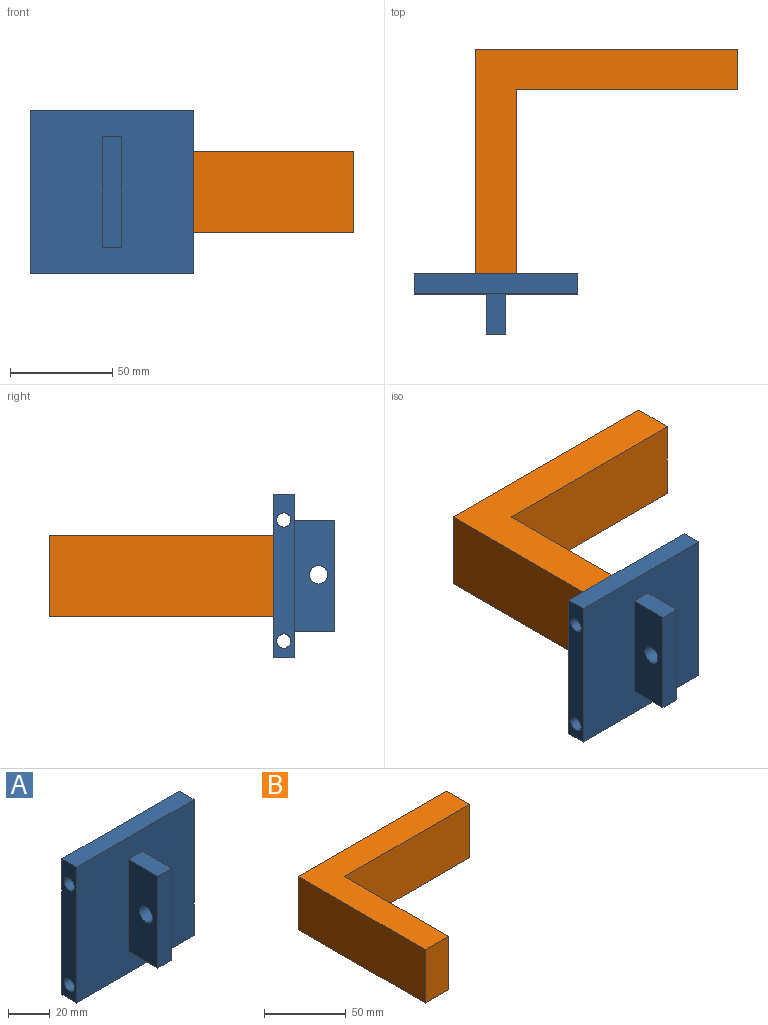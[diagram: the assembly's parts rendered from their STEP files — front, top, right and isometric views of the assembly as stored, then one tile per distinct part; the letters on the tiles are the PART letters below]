
ASSEMBLY  parts=2 mates=1
PART A: 14 faces, bbox 80x30x80 mm
  f0: plane 80x80mm, normal (0,-1,0), area 5884.6mm2, adj f1,f2,f3,f4,f6,f7,f8,f9
  f1: plane 80x10mm, normal (-1,0,0), area 723mm2, adj f0,f2,f4,f5,f11,f12
  f2: plane 80x10mm, normal (0,0,-1), area 800mm2, adj f0,f1,f3,f5
  f3: plane 80x10mm, normal (1,0,0), area 723mm2, adj f0,f2,f4,f5,f11,f12
  f4: plane 80x10mm, normal (0,0,1), area 800mm2, adj f0,f1,f3,f5
  f5: plane 80x80mm, normal (0,1,0), area 6400mm2, adj f1,f2,f3,f4
  f6: plane 54.11x20mm, normal (-1,0,0), area 1018.5mm2, adj f0,f7,f9,f10,f13
  f7: plane 20x9.53mm, normal (0,0,-1), area 190.5mm2, adj f0,f6,f8,f10
  f8: plane 54.11x20mm, normal (1,0,0), area 1018.5mm2, adj f0,f7,f9,f10,f13
  f9: plane 20x9.53mm, normal (0,0,1), area 190.5mm2, adj f0,f6,f8,f10
  f10: plane 54.11x9.53mm, normal (0,-1,0), area 515.4mm2, adj f6,f7,f8,f9
  f11: cylinder r=3.5mm len=80mm, axis (1,0,0), area 1759.3mm2, adj f1,f3
  f12: cylinder r=3.5mm len=80mm, axis (1,0,0), area 1759.3mm2, adj f1,f3
  f13: cylinder r=4.5mm len=9.53mm, axis (1,0,0), area 269.3mm2, adj f6,f8
PART B: 8 faces, bbox 128.4x110x40 mm
  f0: plane 110x40mm, normal (-1,0,0), area 4400mm2, adj f1,f5,f6,f7
  f1: plane 40x20mm, normal (0,-1,0), area 800mm2, adj f0,f2,f6,f7
  f2: plane 90x40mm, normal (1,0,0), area 3600mm2, adj f1,f3,f6,f7
  f3: plane 108.38x40mm, normal (0,-1,0), area 4335.2mm2, adj f2,f4,f6,f7
  f4: plane 40x20mm, normal (1,0,0), area 800mm2, adj f3,f5,f6,f7
  f5: plane 128.38x40mm, normal (0,1,0), area 5135.2mm2, adj f0,f4,f6,f7
  f6: plane 128.38x110mm, normal (0,0,1), area 4367.6mm2, adj f0,f1,f2,f3,f4,f5
  f7: plane 128.38x110mm, normal (0,0,-1), area 4367.6mm2, adj f0,f1,f2,f3,f4,f5
PLACE A t=(-89.78,-93.84,67.78)mm
PLACE B t=(-59.78,-93.84,87.78)mm
MATE fastened B.f1 <-> A.f5  axis (0,-1,0) through (-49.78,-93.84,107.78)mm
